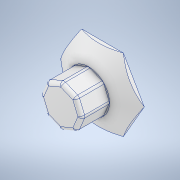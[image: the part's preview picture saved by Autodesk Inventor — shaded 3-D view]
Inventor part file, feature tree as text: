
AUTODESK INVENTOR PART (.ipt)
format: ipt  version: 2022 (Build 260153000, 153)  size: 272,384 bytes
history: native  units: in
note: dims shown in document units (in); Inventor stores cm internally (conversion verified against a paired STEP export)
features: extrude x6, sketch x6, revolve x1, shell x1, fillet x1
ambient origin geometry x8: Origin, YZ Plane, XZ Plane, XY Plane, X Axis, Y Axis, Z Axis, Center Point
bodies: Solid1 (feature_tree)
feature tree (15):
  extrude  "Extrusion1"  Depth=0.5in TaperAngle=0.0deg
  revolve  "Revolution1"  [1 undecoded]
  extrude  "Extrusion2"  Depth=3.0in TaperAngle=0.0deg
  sketch  "Sketch5"  dims[d8=0.5in d9=0.0in d11=0.05in d20=0.63in]
  extrude  "Extrusion3"  Depth=0.05in
  shell  "Shell1"  Thickness=0.63in
  extrude  "Extrusion4"  Depth=0.63in
  extrude  "Extrusion5"  Depth=0.0625in
  extrude  "Extrusion6"  Depth=0.0625in
  fillet  "Fillet2"  Radius=0.02in
  sketch  "Sketch1"  dims[d0=0.75in d1=0.5in d2=0.0in]
  sketch  "Sketch2"  dims[d3=0.25in d4=0.75in]
  sketch  "Sketch3"  dims[d5=90.0deg d6=3.0in d7=0.0in]
  sketch  "Sketch6"  dims[d21=0.04in d22=0.63in]
  sketch  "Sketch7"  dims[d23=0.04in d24=0.02in d25=0.02in d26=0.02in d27=0.02in d28=0.02in d29=0.02in d30=0.63in d31=0.04in d32=0.0in d33=0.225in d34=0.3in d35=0.5in d36=0.0in d37=0.5in d38=0.0in d39=0.5in d40=0.0in d41=0.0625in d10=0.0in d12=0.0in d13=0.0in d42=0.0344in]
note: 1 required parameter value undecoded (feature->parameter linkage not recoverable at this tier; creation-order binding heuristic only, values carry confidence <= 0.55)
